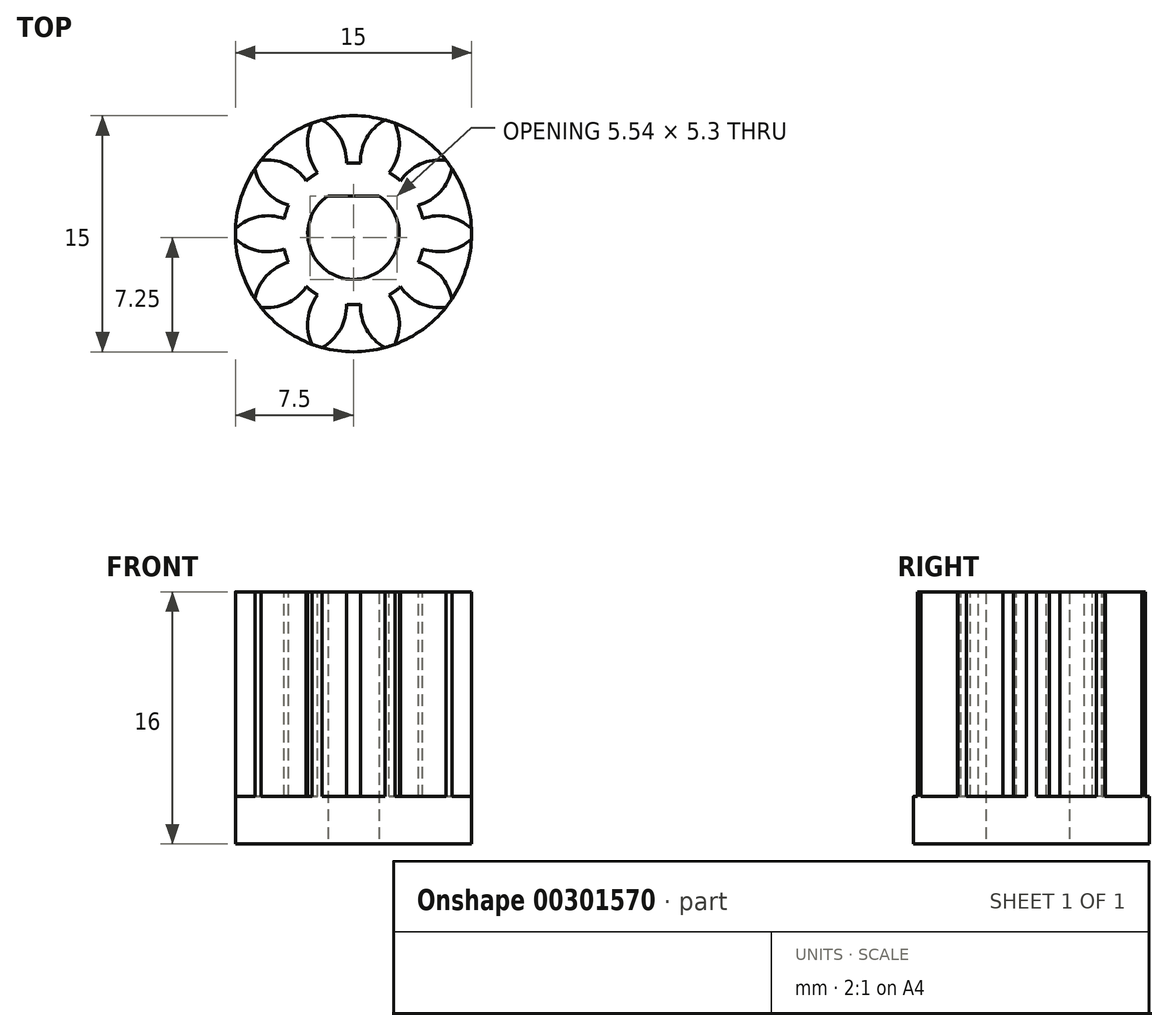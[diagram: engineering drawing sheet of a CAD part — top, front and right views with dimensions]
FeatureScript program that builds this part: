
annotation { "Feature Type Name" : "Feature", "Feature Type Description" : "" }
export const myFeature = defineFeature(function(context is Context, id is Id, definition is map)
    precondition{}
    {
        {
            var Q0;
            Q0=qCreatedBy(makeId("Top.planeOp"),FACE);
            var sketch = newSketch(context, id + "F0", { "sketchPlane" : qUnion([Q0])});
            skArc(sketch, "E0", {"start": v(-1.63, 2.4) * mm, "mid": v(0, -2.9) * mm, "end": v(1.63, 2.4) * mm});
            skCircle(sketch, "E1", {"center": v(0, 0) * mm, "radius": 7.5 * mm});
            skLineSegment(sketch, "E2", {"start": v(1.63, 2.4) * mm, "end": v(-1.63, 2.4) * mm});
            skSolve(sketch);
        }
        {
            var Q0;
            Q0=makeQuery(id+"F0.imprint","IMPRINT",FACE,{"disambiguationData":[TD([[makeQuery(id+"F0.imprint","IMPRINT",EDGE,{"derivedFrom":sQuery(id+"F0.wireOp",EDGE,"E0")}),-1.0]])]});
            extrude(context, id + "F1", {"entities" : qUnion([Q0]), "depth" : 16 * mm});
        }
        {
            var Q0;
            Q0=makeQuery(id+"F1.opExtrude","CAP_FACE",FACE,{"disambiguationData":[OSD([sQuery(id+"F0.wireOp",EDGE,"E0"),sQuery(id+"F0.wireOp",EDGE,"E1"),sQuery(id+"F0.wireOp",EDGE,"E2")])],"isStart":false});
            var sketch = newSketch(context, id + "F2", { "sketchPlane" : qUnion([Q0])});
            skArc(sketch, "E3", {"start": v(2, 7.23) * mm, "mid": v(0, 7.5) * mm, "end": v(-2, 7.23) * mm});
            skArc(sketch, "E4", {"start": v(0.45, 4.48) * mm, "mid": v(0, 4.5) * mm, "end": v(-0.45, 4.48) * mm});
            skArc(sketch, "E5", {"start": v(-0.45, 4.48) * mm, "mid": v(-0.83, 6.07) * mm, "end": v(-2, 7.23) * mm});
            skArc(sketch, "E6.MirrorCS", {"start": v(0.45, 4.48) * mm, "mid": v(0.83, 6.07) * mm, "end": v(2, 7.23) * mm});
            skSolve(sketch);
        }
        {
            var Q0;
            Q0=makeQuery(id+"F2.imprint","IMPRINT",FACE,{"disambiguationData":[TD([[makeQuery(id+"F2.imprint","IMPRINT",EDGE,{"derivedFrom":sQuery(id+"F2.wireOp",EDGE,"E3")}),1.0]])]});
            extrude(context, id + "F3", {"entities" : qUnion([Q0]), "operationType" : NewBodyOperationType.REMOVE, "endBound" : BoundingType.UP_TO_NEXT, "oppositeDirection" : true, "depth" : 25 * mm});
        }
        {
            var Q0;
            Q0=makeQuery(id+"F3.boolean.opBoolean","COPY",FACE,{"derivedFrom":makeQuery(id+"F3.opExtrude","SWEPT_FACE",FACE,{"disambiguationData":[OSD([sQuery(id+"F2.wireOp",EDGE,"E5")])]})});
            var Q1;
            Q1=makeQuery(id+"F3.boolean.opBoolean","COPY",FACE,{"derivedFrom":makeQuery(id+"F3.opExtrude","SWEPT_FACE",FACE,{"disambiguationData":[OSD([sQuery(id+"F2.wireOp",EDGE,"E4")])]})});
            var Q2;
            Q2=makeQuery(id+"F3.boolean.opBoolean","COPY",FACE,{"derivedFrom":makeQuery(id+"F3.opExtrude","SWEPT_FACE",FACE,{"disambiguationData":[OSD([sQuery(id+"F2.wireOp",EDGE,"E6.MirrorCS")])]})});
            var Q3;
            Q3=makeQuery(id+"F1.opExtrude","SWEPT_FACE",FACE,{"disambiguationData":[OSD([sQuery(id+"F0.wireOp",EDGE,"E1")])]});
            circularPattern(context, id + "F4", {"patternType" : PatternType.FACE, "faces" : qUnion([Q0, Q1, Q2]), "axis" : qUnion([Q3]), "angle" : 360 * degree, "instanceCount" : 10, "equalSpace" : true});
        }
        {
            var Q0;
            Q0=qCreatedBy(makeId("Top.planeOp"),FACE);
            var sketch = newSketch(context, id + "F5", { "sketchPlane" : qUnion([Q0])});
            skCircle(sketch, "E7", {"center": v(0, 0) * mm, "radius": 7.5 * mm});
            skSolve(sketch);
        }
        {
            var Q0;
            Q0=makeQuery(id+"F5.imprint","IMPRINT",FACE,{"disambiguationData":[TD([[makeQuery(id+"F5.imprint","IMPRINT",EDGE,{"derivedFrom":sQuery(id+"F5.wireOp",EDGE,"E7")}),1.0]])]});
            extrude(context, id + "F6", {"entities" : qUnion([Q0]), "operationType" : NewBodyOperationType.ADD, "depth" : 3 * mm});
        }
        {
            var Q0;
            Q0=makeQuery(id+"F6.boolean.opBoolean","SPLIT",FACE,{"disambiguationData":[TD([makeQuery(id+"F1.opExtrude","SWEPT_FACE",FACE,{"disambiguationData":[OSD([sQuery(id+"F0.wireOp",EDGE,"E0")])]})])],"derivedFrom":makeQuery(id+"F6.opExtrude","CAP_FACE",FACE,{"disambiguationData":[OSD([sQuery(id+"F5.wireOp",EDGE,"E7")])],"isStart":false})});
            var sketch = newSketch(context, id + "F7", { "sketchPlane" : qUnion([Q0])});
            skArc(sketch, "E8", {"start": v(-1.63, 2.4) * mm, "mid": v(0, -2.9) * mm, "end": v(1.63, 2.4) * mm});
            skLineSegment(sketch, "E9", {"start": v(1.63, 2.4) * mm, "end": v(-1.63, 2.4) * mm});
            skSolve(sketch);
        }
        {
            var Q0;
            Q0=qSketchRegion(id+"F7",true);
            extrude(context, id + "F8", {"entities" : qUnion([Q0]), "operationType" : NewBodyOperationType.REMOVE, "endBound" : BoundingType.UP_TO_NEXT, "oppositeDirection" : true, "depth" : 25 * mm});
        }
    });
